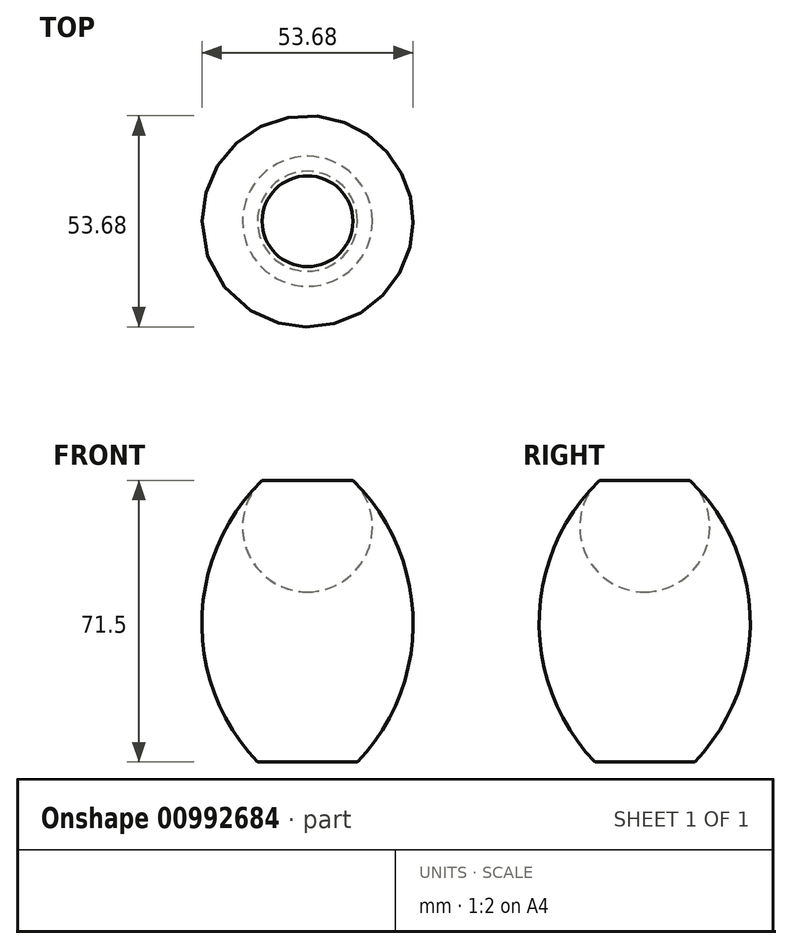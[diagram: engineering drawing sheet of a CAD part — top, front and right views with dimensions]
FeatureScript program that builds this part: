
annotation { "Feature Type Name" : "Feature", "Feature Type Description" : "" }
export const myFeature = defineFeature(function(context is Context, id is Id, definition is map)
    precondition{}
    {
        {
            var Q0;
            Q0=qCreatedBy(makeId("Front.planeOp"),FACE);
            var sketch = newSketch(context, id + "F0", { "sketchPlane" : qUnion([Q0])});
            skLineSegment(sketch, "E0", {"start": v(0, 0) * mm, "end": v(12.7, 0) * mm});
            skLineSegment(sketch, "E1", {"start": v(0, 0) * mm, "end": v(0, 76.2) * mm});
            skCircle(sketch, "E2", {"center": v(0, 59.69) * mm, "radius": 16.51 * mm});
            skArc(sketch, "E3", {"start": v(12.7, 0) * mm, "mid": v(26.83, 35.99) * mm, "end": v(11.54, 71.5) * mm});
            skSolve(sketch);
        }
        {
            var Q0;
            {var subQ0=sQuery(id+"F0.wireOp",EDGE,"E0");Q0=makeQuery(id+"F0.imprint","IMPRINT",FACE,{"disambiguationData":[TD([[makeQuery(id+"F0.imprint","IMPRINT",EDGE,{"derivedFrom":subQ0}),1.0]])]});}
            var Q1;
            {var subQ0=sQuery(id+"F0.wireOp",EDGE,"E2");var subQ1=sQuery(id+"F0.wireOp",EDGE,"E1");var subQ2=makeQuery(id+"F0.imprint","INTERSECT",VERTEX,{"disambiguationData":[OD(0.0)],"derivedFrom":[subQ1,subQ0]});Q1=makeQuery(id+"F0.imprint","IMPRINT",FACE,{"disambiguationData":[TD([[makeQuery(id+"F0.imprint","IMPRINT",EDGE,{"disambiguationData":[TD([[subQ2,1.0]])],"derivedFrom":subQ1}),-1.0]])]});}
            var Q2;
            Q2=sQuery(id+"F0.wireOp",EDGE,"E1");
            revolve(context, id + "F1", {"surfaceOperationType" : NewSurfaceOperationType.NEW, "entities" : qUnion([Q0, Q1]), "axis" : qUnion([Q2]), "revolveType" : RevolveType.FULL});
        }
    });
